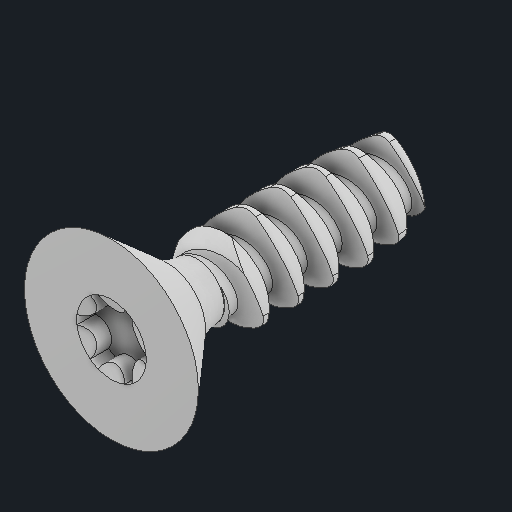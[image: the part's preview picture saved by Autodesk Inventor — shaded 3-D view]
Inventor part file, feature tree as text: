
AUTODESK INVENTOR PART (.ipt)
format: ipt  version: 2025 (Build 290162000, 162)  size: 445,952 bytes
history: native  units: in
note: dims shown in document units (in); Inventor stores cm internally (conversion verified against a paired STEP export)
features: revolve x1
ambient origin geometry x8: Origin, YZ Plane, XZ Plane, XY Plane, X Axis, Y Axis, Z Axis, Center Point
bodies: Solid1 (feature_tree)
feature tree (1):
  revolve  "Revolve3"  [1 undecoded]
note: 1 required parameter value undecoded (feature->parameter linkage not recoverable at this tier; creation-order binding heuristic only, values carry confidence <= 0.55)
